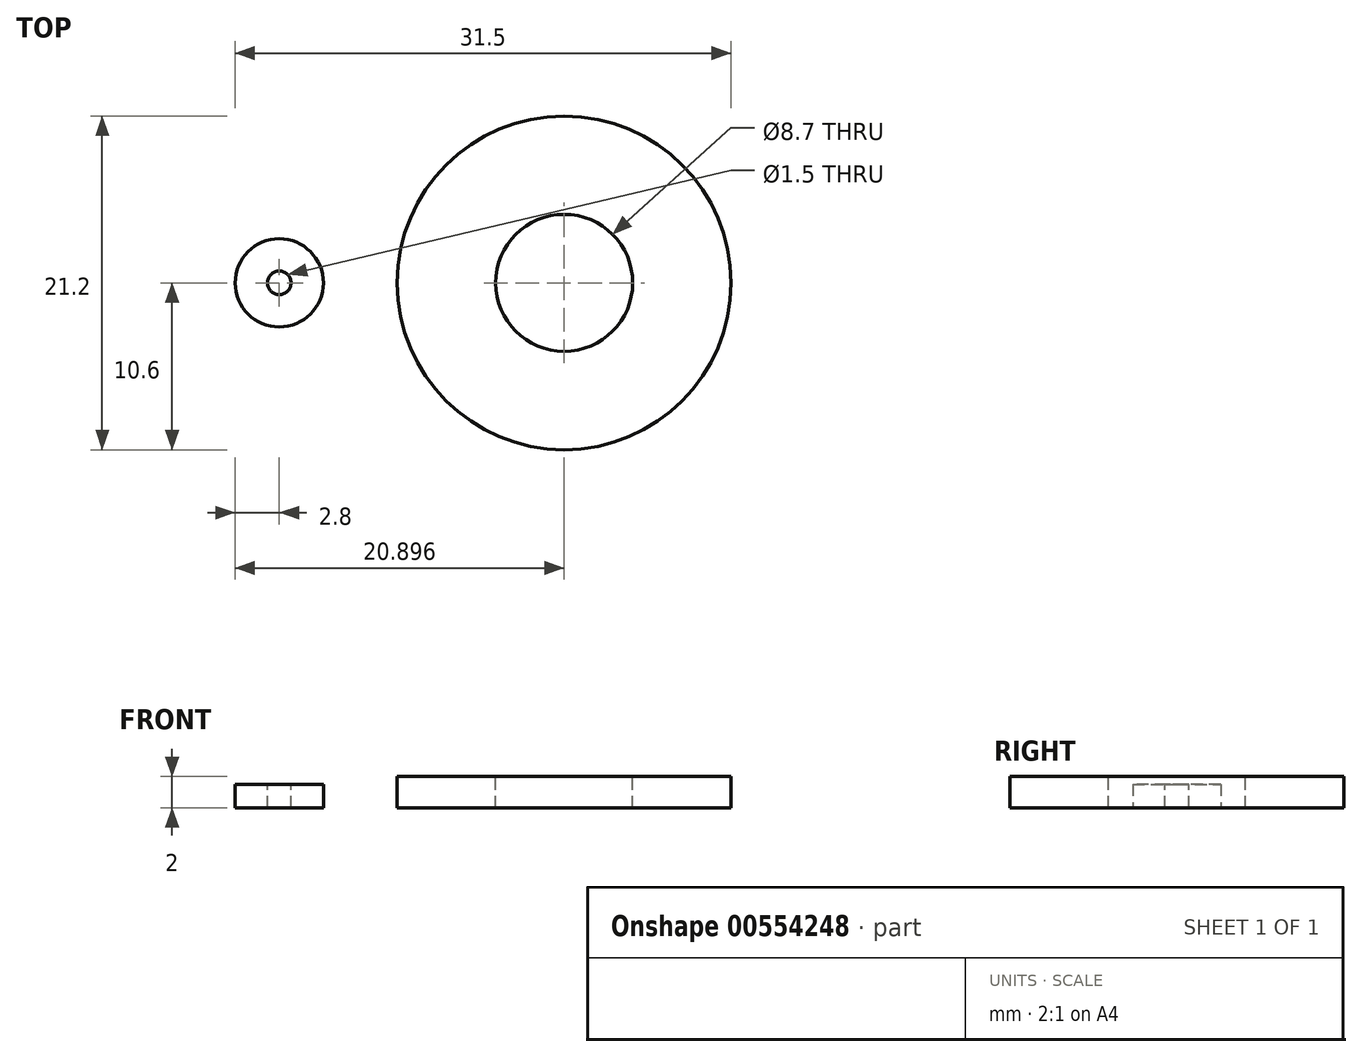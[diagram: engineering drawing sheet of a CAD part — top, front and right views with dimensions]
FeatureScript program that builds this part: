
annotation { "Feature Type Name" : "Feature", "Feature Type Description" : "" }
export const myFeature = defineFeature(function(context is Context, id is Id, definition is map)
    precondition{}
    {
        {
            var Q0;
            Q0=qCreatedBy(makeId("Top.planeOp"),FACE);
            var sketch = newSketch(context, id + "F0", { "sketchPlane" : qUnion([Q0])});
            skCircle(sketch, "E0", {"center": v(0, 0) * mm, "radius": 2.8 * mm});
            skSolve(sketch);
        }
        {
            var Q0;
            Q0=makeQuery(id+"F0.imprint","IMPRINT",FACE,{"disambiguationData":[TD([[makeQuery(id+"F0.imprint","IMPRINT",EDGE,{"derivedFrom":sQuery(id+"F0.wireOp",EDGE,"E0")}),1.0]])]});
            extrude(context, id + "F1", {"entities" : qUnion([Q0]), "depth" : 1.5 * mm});
        }
        {
            var Q0;
            Q0=makeQuery(id+"F1.opExtrude","CAP_FACE",FACE,{"disambiguationData":[OSD([sQuery(id+"F0.wireOp",EDGE,"E0")])],"isStart":false});
            var sketch = newSketch(context, id + "F2", { "sketchPlane" : qUnion([Q0])});
            skCircle(sketch, "E1", {"center": v(0, 0) * mm, "radius": 0.75 * mm});
            skSolve(sketch);
        }
        {
            var Q0;
            Q0=makeQuery(id+"F2.imprint","IMPRINT",FACE,{"disambiguationData":[TD([[makeQuery(id+"F2.imprint","IMPRINT",EDGE,{"derivedFrom":sQuery(id+"F2.wireOp",EDGE,"E1")}),1.0]])]});
            extrude(context, id + "F3", {"entities" : qUnion([Q0]), "operationType" : NewBodyOperationType.REMOVE, "oppositeDirection" : true, "depth" : 25 * mm});
        }
        {
            var Q0;
            Q0=qCreatedBy(makeId("Top.planeOp"),FACE);
            var sketch = newSketch(context, id + "F4", { "sketchPlane" : qUnion([Q0])});
            skCircle(sketch, "E2", {"center": v(18.1, 0) * mm, "radius": 10.6 * mm});
            skSolve(sketch);
        }
        {
            var Q0;
            Q0=qSketchRegion(id+"F4",true);
            extrude(context, id + "F5", {"entities" : qUnion([Q0]), "depth" : 2 * mm});
        }
        {
            var Q0;
            Q0=makeQuery(id+"F5.opExtrude","CAP_FACE",FACE,{"disambiguationData":[OSD([sQuery(id+"F4.wireOp",EDGE,"E2")])],"isStart":false});
            var sketch = newSketch(context, id + "F6", { "sketchPlane" : qUnion([Q0])});
            skCircle(sketch, "E3", {"center": v(18.1, 0) * mm, "radius": 4.35 * mm});
            skSolve(sketch);
        }
        {
            var Q0;
            Q0=makeQuery(id+"F6.imprint","IMPRINT",FACE,{"disambiguationData":[TD([[makeQuery(id+"F6.imprint","IMPRINT",EDGE,{"derivedFrom":sQuery(id+"F6.wireOp",EDGE,"E3")}),1.0]])]});
            extrude(context, id + "F7", {"entities" : qUnion([Q0]), "operationType" : NewBodyOperationType.REMOVE, "oppositeDirection" : true, "depth" : 25 * mm});
        }
    });
